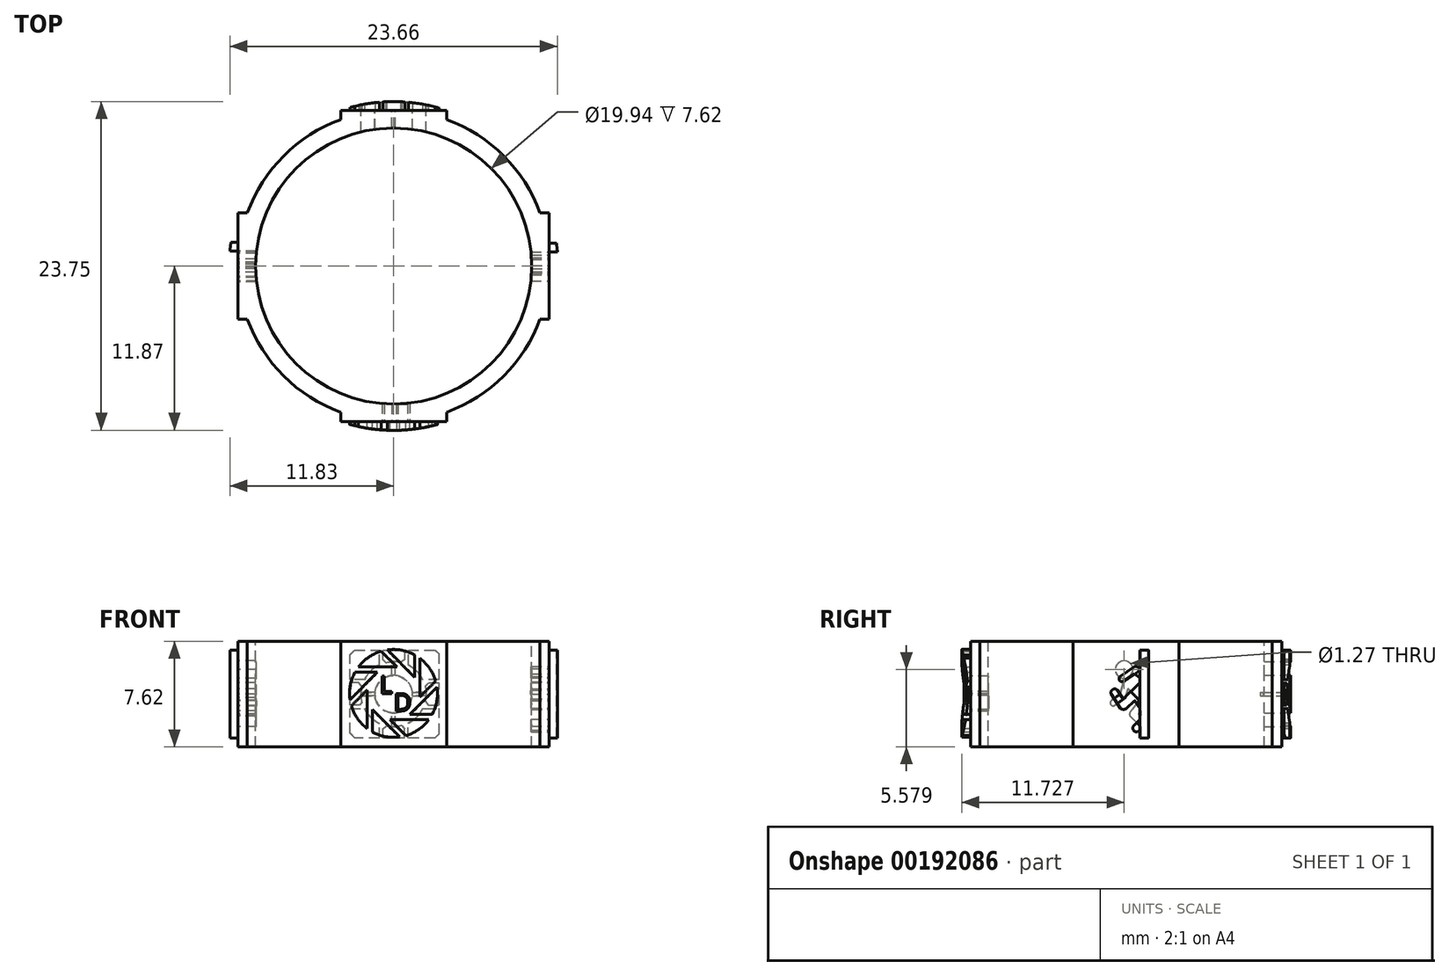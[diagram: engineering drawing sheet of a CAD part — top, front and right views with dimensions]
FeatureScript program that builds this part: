
annotation { "Feature Type Name" : "Feature", "Feature Type Description" : "" }
export const myFeature = defineFeature(function(context is Context, id is Id, definition is map)
    precondition{}
    {
        {
            var Q0;
            Q0=qCreatedBy(makeId("Front.planeOp"),FACE);
            var sketch = newSketch(context, id + "F0", { "sketchPlane" : qUnion([Q0])});
            skLineSegment(sketch, "E0.bottom", {"start": v(-11.24, 3.81) * mm, "end": v(11.24, 3.81) * mm});
            skLineSegment(sketch, "E0.top", {"start": v(-11.24, -3.81) * mm, "end": v(11.24, -3.81) * mm});
            skLineSegment(sketch, "E0.left", {"start": v(-11.24, 3.81) * mm, "end": v(-11.24, -3.81) * mm});
            skLineSegment(sketch, "E0.right", {"start": v(11.24, 3.81) * mm, "end": v(11.24, -3.81) * mm});
            skLineSegment(sketch, "E1.0", {"start": v(-2.54, 1.9) * mm, "end": v(0.25, 1.9) * mm});
            skLineSegment(sketch, "E1.1", {"start": v(0.79, 1.9) * mm, "end": v(1.52, 1.17) * mm});
            skLineSegment(sketch, "E1.2", {"start": v(1.9, 0.79) * mm, "end": v(1.9, -0.25) * mm});
            skLineSegment(sketch, "E1.3", {"start": v(1.9, -0.79) * mm, "end": v(1.17, -1.52) * mm});
            skLineSegment(sketch, "E1.4", {"start": v(0.79, -1.9) * mm, "end": v(-0.25, -1.9) * mm});
            skLineSegment(sketch, "E1.5", {"start": v(-0.79, -1.9) * mm, "end": v(-1.52, -1.17) * mm});
            skLineSegment(sketch, "E1.6", {"start": v(-1.9, -0.79) * mm, "end": v(-1.9, 0.25) * mm});
            skLineSegment(sketch, "E1.7", {"start": v(-1.9, 0.79) * mm, "end": v(-1.17, 1.52) * mm});
            skArc(sketch, "E2", {"start": v(-2.79, 1.52) * mm, "mid": v(-3.12, 0.57) * mm, "end": v(-3.14, -0.45) * mm});
            skLineSegment(sketch, "E3.0", {"start": v(-2.79, 1.52) * mm, "end": v(-1.17, 1.52) * mm});
            skLineSegment(sketch, "E4.1.0", {"start": v(-3.05, -0.9) * mm, "end": v(-1.9, 0.25) * mm});
            skLineSegment(sketch, "E4.1.1", {"start": v(-3.14, -0.45) * mm, "end": v(-1.17, 1.52) * mm});
            skLineSegment(sketch, "E4.2.0", {"start": v(-1.52, -2.79) * mm, "end": v(-1.52, -1.17) * mm});
            skLineSegment(sketch, "E4.2.1", {"start": v(-1.9, -2.54) * mm, "end": v(-1.9, 0.25) * mm});
            skLineSegment(sketch, "E4.3.0", {"start": v(0.9, -3.05) * mm, "end": v(-0.25, -1.9) * mm});
            skLineSegment(sketch, "E4.3.1", {"start": v(0.45, -3.14) * mm, "end": v(-1.52, -1.17) * mm});
            skLineSegment(sketch, "E4.4.0", {"start": v(2.79, -1.52) * mm, "end": v(1.17, -1.52) * mm});
            skLineSegment(sketch, "E4.4.1", {"start": v(2.54, -1.9) * mm, "end": v(-0.25, -1.9) * mm});
            skLineSegment(sketch, "E4.5.0", {"start": v(3.05, 0.9) * mm, "end": v(1.9, -0.25) * mm});
            skLineSegment(sketch, "E4.5.1", {"start": v(3.14, 0.45) * mm, "end": v(1.17, -1.52) * mm});
            skLineSegment(sketch, "E4.6.0", {"start": v(1.52, 2.79) * mm, "end": v(1.52, 1.17) * mm});
            skLineSegment(sketch, "E4.6.1", {"start": v(1.9, 2.54) * mm, "end": v(1.9, -0.25) * mm});
            skLineSegment(sketch, "E4.7.0", {"start": v(-0.9, 3.05) * mm, "end": v(0.25, 1.9) * mm});
            skLineSegment(sketch, "E4.7.1", {"start": v(-0.45, 3.14) * mm, "end": v(1.52, 1.17) * mm});
            skArc(sketch, "E5.trimOffspring", {"start": v(-0.9, 3.05) * mm, "mid": v(-1.8, 2.6) * mm, "end": v(-2.54, 1.9) * mm});
            skArc(sketch, "E6.trimOffspring", {"start": v(1.52, 2.79) * mm, "mid": v(0.57, 3.12) * mm, "end": v(-0.45, 3.14) * mm});
            skArc(sketch, "E7.trimOffspring", {"start": v(3.05, 0.9) * mm, "mid": v(2.6, 1.8) * mm, "end": v(1.9, 2.54) * mm});
            skArc(sketch, "E8.trimOffspring", {"start": v(2.79, -1.52) * mm, "mid": v(3.12, -0.57) * mm, "end": v(3.14, 0.45) * mm});
            skArc(sketch, "E9.trimOffspring", {"start": v(0.9, -3.05) * mm, "mid": v(1.8, -2.6) * mm, "end": v(2.54, -1.9) * mm});
            skArc(sketch, "E10.trimOffspring", {"start": v(-1.52, -2.79) * mm, "mid": v(-0.57, -3.12) * mm, "end": v(0.45, -3.14) * mm});
            skArc(sketch, "E11.trimOffspring", {"start": v(-3.05, -0.9) * mm, "mid": v(-2.6, -1.8) * mm, "end": v(-1.9, -2.54) * mm});
            skText(sketch, "E12", { "text": "L", "fontName": "OpenSans-Regular.ttf"});
            skText(sketch, "E13", { "text": "D", "fontName": "OpenSans-Regular.ttf"});
            const initialGuessF0  = {"E12": [-0.00099, 0, 1, 0, 0.00127], "E13": [0, -0.00127, 1, 0, 0.00127]};
            skSetInitialGuess(sketch, initialGuessF0);
            skSolve(sketch);
        }
        {
            var Q0;
            Q0=makeQuery(id+"F0.imprint","IMPRINT",FACE,{"disambiguationData":[TD([[makeQuery(id+"F0.imprint","IMPRINT",EDGE,{"derivedFrom":sQuery(id+"F0.wireOp",EDGE,"E0.bottom")}),-1.0]])]});
            var Q1;
            Q1=makeQuery(id+"F0.imprint","IMPRINT",FACE,{"disambiguationData":[TD([[makeQuery(id+"F0.imprint","IMPRINT",EDGE,{"derivedFrom":sQuery(id+"F0.wireOp",EDGE,"E13.sketch_text.stroke-7")}),1.0]])]});
            var Q2;
            Q2=makeQuery(id+"F0.imprint","IMPRINT",FACE,{"disambiguationData":[TD([[makeQuery(id+"F0.imprint","IMPRINT",EDGE,{"derivedFrom":sQuery(id+"F0.wireOp",EDGE,"E1.0")}),1.0]])]});
            var Q3;
            {var subQ0=sQuery(id+"F0.wireOp",EDGE,"E2");Q3=makeQuery(id+"F0.imprint","IMPRINT",FACE,{"disambiguationData":[TD([[makeQuery(id+"F0.imprint","IMPRINT",EDGE,{"derivedFrom":subQ0}),1.0]])]});}
            var Q4;
            {var subQ0=sQuery(id+"F0.wireOp",EDGE,"E4.1.0");Q4=makeQuery(id+"F0.imprint","IMPRINT",FACE,{"disambiguationData":[TD([[makeQuery(id+"F0.imprint","IMPRINT",EDGE,{"derivedFrom":subQ0}),-1.0]])]});}
            var Q5;
            {var subQ0=sQuery(id+"F0.wireOp",EDGE,"E4.2.0");Q5=makeQuery(id+"F0.imprint","IMPRINT",FACE,{"disambiguationData":[TD([[makeQuery(id+"F0.imprint","IMPRINT",EDGE,{"derivedFrom":subQ0}),-1.0]])]});}
            var Q6;
            {var subQ0=sQuery(id+"F0.wireOp",EDGE,"E4.3.0");Q6=makeQuery(id+"F0.imprint","IMPRINT",FACE,{"disambiguationData":[TD([[makeQuery(id+"F0.imprint","IMPRINT",EDGE,{"derivedFrom":subQ0}),-1.0]])]});}
            var Q7;
            {var subQ0=sQuery(id+"F0.wireOp",EDGE,"E4.4.0");Q7=makeQuery(id+"F0.imprint","IMPRINT",FACE,{"disambiguationData":[TD([[makeQuery(id+"F0.imprint","IMPRINT",EDGE,{"derivedFrom":subQ0}),-1.0]])]});}
            var Q8;
            {var subQ0=sQuery(id+"F0.wireOp",EDGE,"E4.5.0");Q8=makeQuery(id+"F0.imprint","IMPRINT",FACE,{"disambiguationData":[TD([[makeQuery(id+"F0.imprint","IMPRINT",EDGE,{"derivedFrom":subQ0}),-1.0]])]});}
            var Q9;
            {var subQ0=sQuery(id+"F0.wireOp",EDGE,"E4.6.0");Q9=makeQuery(id+"F0.imprint","IMPRINT",FACE,{"disambiguationData":[TD([[makeQuery(id+"F0.imprint","IMPRINT",EDGE,{"derivedFrom":subQ0}),-1.0]])]});}
            var Q10;
            Q10=makeQuery(id+"F0.imprint","IMPRINT",FACE,{"disambiguationData":[TD([[makeQuery(id+"F0.imprint","IMPRINT",EDGE,{"derivedFrom":sQuery(id+"F0.wireOp",EDGE,"E12.sketch_text.stroke-0")}),-1.0]])]});
            var Q11;
            Q11=makeQuery(id+"F0.imprint","IMPRINT",FACE,{"disambiguationData":[TD([[makeQuery(id+"F0.imprint","IMPRINT",EDGE,{"derivedFrom":sQuery(id+"F0.wireOp",EDGE,"E13.sketch_text.stroke-0")}),-1.0]])]});
            extrude(context, id + "F1", {"entities" : qUnion([Q0, Q1, Q2, Q3, Q4, Q5, Q6, Q7, Q8, Q9, Q10, Q11]), "depth" : 22.48 * mm});
        }
        {
            var Q0;
            Q0=makeQuery(id+"F1.opExtrude","CAP_FACE",FACE,{"disambiguationData":[OSD([sQuery(id+"F0.wireOp",EDGE,"E0.bottom"),sQuery(id+"F0.wireOp",EDGE,"E0.top"),sQuery(id+"F0.wireOp",EDGE,"E0.left"),sQuery(id+"F0.wireOp",EDGE,"E0.right")])],"isStart":false});
            var sketch = newSketch(context, id + "F2", { "sketchPlane" : qUnion([Q0])});
            skLineSegment(sketch, "E14.bottom", {"start": v(-11.25, 3.86) * mm, "end": v(11.23, 3.86) * mm});
            skLineSegment(sketch, "E14.top", {"start": v(-11.25, -3.76) * mm, "end": v(11.23, -3.76) * mm});
            skLineSegment(sketch, "E14.left", {"start": v(-11.25, 3.86) * mm, "end": v(-11.25, -3.76) * mm});
            skLineSegment(sketch, "E14.right", {"start": v(11.23, 3.86) * mm, "end": v(11.23, -3.76) * mm});
            skLineSegment(sketch, "E15.0", {"start": v(-2.55, 1.96) * mm, "end": v(0.24, 1.96) * mm});
            skLineSegment(sketch, "E15.1", {"start": v(0.78, 1.96) * mm, "end": v(1.52, 1.22) * mm});
            skLineSegment(sketch, "E15.2", {"start": v(1.9, 0.84) * mm, "end": v(1.9, -0.2) * mm});
            skLineSegment(sketch, "E15.3", {"start": v(1.9, -0.74) * mm, "end": v(1.16, -1.47) * mm});
            skLineSegment(sketch, "E15.4", {"start": v(0.78, -1.85) * mm, "end": v(-0.26, -1.85) * mm});
            skLineSegment(sketch, "E15.5", {"start": v(-0.8, -1.85) * mm, "end": v(-1.53, -1.12) * mm});
            skLineSegment(sketch, "E15.6", {"start": v(-1.91, -0.74) * mm, "end": v(-1.91, 0.3) * mm});
            skLineSegment(sketch, "E15.7", {"start": v(-1.91, 0.84) * mm, "end": v(-1.18, 1.58) * mm});
            skArc(sketch, "E16", {"start": v(-2.8, 1.58) * mm, "mid": v(-3.13, 0.62) * mm, "end": v(-3.15, -0.4) * mm});
            skLineSegment(sketch, "E17.0", {"start": v(-2.8, 1.58) * mm, "end": v(-1.18, 1.58) * mm});
            skLineSegment(sketch, "E18.1.0", {"start": v(-3.05, -0.84) * mm, "end": v(-1.91, 0.3) * mm});
            skLineSegment(sketch, "E18.1.1", {"start": v(-3.15, -0.4) * mm, "end": v(-1.18, 1.58) * mm});
            skLineSegment(sketch, "E18.2.0", {"start": v(-1.53, -2.73) * mm, "end": v(-1.53, -1.12) * mm});
            skLineSegment(sketch, "E18.2.1", {"start": v(-1.91, -2.49) * mm, "end": v(-1.91, 0.3) * mm});
            skLineSegment(sketch, "E18.3.0", {"start": v(0.88, -3) * mm, "end": v(-0.26, -1.85) * mm});
            skLineSegment(sketch, "E18.3.1", {"start": v(0.44, -3.1) * mm, "end": v(-1.53, -1.12) * mm});
            skLineSegment(sketch, "E18.4.0", {"start": v(2.78, -1.47) * mm, "end": v(1.16, -1.47) * mm});
            skLineSegment(sketch, "E18.4.1", {"start": v(2.53, -1.85) * mm, "end": v(-0.26, -1.85) * mm});
            skLineSegment(sketch, "E18.5.0", {"start": v(3.04, 0.94) * mm, "end": v(1.9, -0.2) * mm});
            skLineSegment(sketch, "E18.5.1", {"start": v(3.14, 0.5) * mm, "end": v(1.16, -1.47) * mm});
            skLineSegment(sketch, "E18.6.0", {"start": v(1.52, 2.84) * mm, "end": v(1.52, 1.22) * mm});
            skLineSegment(sketch, "E18.6.1", {"start": v(1.9, 2.6) * mm, "end": v(1.9, -0.2) * mm});
            skLineSegment(sketch, "E18.7.0", {"start": v(-0.9, 3.1) * mm, "end": v(0.24, 1.96) * mm});
            skLineSegment(sketch, "E18.7.1", {"start": v(-0.46, 3.2) * mm, "end": v(1.52, 1.22) * mm});
            skArc(sketch, "E19.trimOffspring", {"start": v(-0.9, 3.1) * mm, "mid": v(-1.82, 2.66) * mm, "end": v(-2.55, 1.96) * mm});
            skArc(sketch, "E20.trimOffspring", {"start": v(1.52, 2.84) * mm, "mid": v(0.56, 3.18) * mm, "end": v(-0.46, 3.2) * mm});
            skArc(sketch, "E21.trimOffspring", {"start": v(3.04, 0.94) * mm, "mid": v(2.6, 1.86) * mm, "end": v(1.9, 2.6) * mm});
            skArc(sketch, "E22.trimOffspring", {"start": v(2.78, -1.47) * mm, "mid": v(3.12, -0.51) * mm, "end": v(3.14, 0.5) * mm});
            skArc(sketch, "E23.trimOffspring", {"start": v(0.88, -3) * mm, "mid": v(1.8, -2.56) * mm, "end": v(2.53, -1.85) * mm});
            skArc(sketch, "E24.trimOffspring", {"start": v(-1.53, -2.73) * mm, "mid": v(-0.57, -3.07) * mm, "end": v(0.44, -3.1) * mm});
            skArc(sketch, "E25.trimOffspring", {"start": v(-3.05, -0.84) * mm, "mid": v(-2.62, -1.76) * mm, "end": v(-1.91, -2.49) * mm});
            skText(sketch, "E26", { "text": "L", "fontName": "OpenSans-Regular.ttf"});
            skText(sketch, "E27", { "text": "D", "fontName": "OpenSans-Regular.ttf"});
            const initialGuessF2  = {"E26": [-0.001, 5e-05, 1, 0, 0.00127], "E27": [0, -0.00122, 1, 0, 0.00127]};
            skSetInitialGuess(sketch, initialGuessF2);
            skSolve(sketch);
        }
        {
            var Q0;
            {var subQ0=sQuery(id+"F2.wireOp",EDGE,"E16");Q0=makeQuery(id+"F2.imprint","IMPRINT",FACE,{"disambiguationData":[TD([[makeQuery(id+"F2.imprint","IMPRINT",EDGE,{"derivedFrom":subQ0}),1.0]])]});}
            var Q1;
            Q1=makeQuery(id+"F2.imprint","IMPRINT",FACE,{"disambiguationData":[TD([[makeQuery(id+"F2.imprint","IMPRINT",EDGE,{"derivedFrom":sQuery(id+"F2.wireOp",EDGE,"E15.0")}),1.0]])]});
            var Q2;
            {var subQ0=sQuery(id+"F2.wireOp",EDGE,"E18.6.0");Q2=makeQuery(id+"F2.imprint","IMPRINT",FACE,{"disambiguationData":[TD([[makeQuery(id+"F2.imprint","IMPRINT",EDGE,{"derivedFrom":subQ0}),-1.0]])]});}
            var Q3;
            {var subQ0=sQuery(id+"F2.wireOp",EDGE,"E18.5.0");Q3=makeQuery(id+"F2.imprint","IMPRINT",FACE,{"disambiguationData":[TD([[makeQuery(id+"F2.imprint","IMPRINT",EDGE,{"derivedFrom":subQ0}),-1.0]])]});}
            var Q4;
            {var subQ0=sQuery(id+"F2.wireOp",EDGE,"E18.4.0");Q4=makeQuery(id+"F2.imprint","IMPRINT",FACE,{"disambiguationData":[TD([[makeQuery(id+"F2.imprint","IMPRINT",EDGE,{"derivedFrom":subQ0}),-1.0]])]});}
            var Q5;
            {var subQ0=sQuery(id+"F2.wireOp",EDGE,"E18.3.0");Q5=makeQuery(id+"F2.imprint","IMPRINT",FACE,{"disambiguationData":[TD([[makeQuery(id+"F2.imprint","IMPRINT",EDGE,{"derivedFrom":subQ0}),-1.0]])]});}
            var Q6;
            {var subQ0=sQuery(id+"F2.wireOp",EDGE,"E18.2.0");Q6=makeQuery(id+"F2.imprint","IMPRINT",FACE,{"disambiguationData":[TD([[makeQuery(id+"F2.imprint","IMPRINT",EDGE,{"derivedFrom":subQ0}),-1.0]])]});}
            var Q7;
            {var subQ0=sQuery(id+"F2.wireOp",EDGE,"E18.1.0");Q7=makeQuery(id+"F2.imprint","IMPRINT",FACE,{"disambiguationData":[TD([[makeQuery(id+"F2.imprint","IMPRINT",EDGE,{"derivedFrom":subQ0}),-1.0]])]});}
            var Q8;
            Q8=makeQuery(id+"F2.imprint","IMPRINT",FACE,{"disambiguationData":[TD([[makeQuery(id+"F2.imprint","IMPRINT",EDGE,{"derivedFrom":sQuery(id+"F2.wireOp",EDGE,"E26.sketch_text.stroke-0")}),-1.0]])]});
            var Q9;
            Q9=makeQuery(id+"F2.imprint","IMPRINT",FACE,{"disambiguationData":[TD([[makeQuery(id+"F2.imprint","IMPRINT",EDGE,{"derivedFrom":sQuery(id+"F2.wireOp",EDGE,"E27.sketch_text.stroke-0")}),-1.0]])]});
            extrude(context, id + "F3", {"entities" : qUnion([Q0, Q1, Q2, Q3, Q4, Q5, Q6, Q7, Q8, Q9]), "operationType" : NewBodyOperationType.ADD, "depth" : 25.4 * mm});
        }
        {
            var Q0;
            Q0=makeQuery(id+"F1.opExtrude","SWEPT_FACE",FACE,{"disambiguationData":[OSD([sQuery(id+"F0.wireOp",EDGE,"E0.right")])]});
            var sketch = newSketch(context, id + "F4", { "sketchPlane" : qUnion([Q0])});
            skLineSegment(sketch, "E28", {"start": v(-10.23, -2.6) * mm, "end": v(-10.45, -2.73) * mm});
            skLineSegment(sketch, "E29", {"start": v(-10.71, -2.31) * mm, "end": v(-10.23, -1.82) * mm});
            skLineSegment(sketch, "E30", {"start": v(-10.23, -1.82) * mm, "end": v(-10.23, -1.02) * mm});
            skLineSegment(sketch, "E31", {"start": v(-10.23, -1.02) * mm, "end": v(-10.63, -0.46) * mm});
            skLineSegment(sketch, "E32", {"start": v(-10.63, -0.46) * mm, "end": v(-11.22, -1.04) * mm});
            skLineSegment(sketch, "E33", {"start": v(-11.65, -1.04) * mm, "end": v(-12.32, 0) * mm});
            skLineSegment(sketch, "E34", {"start": v(-11.86, 0.3) * mm, "end": v(-11.44, -0.35) * mm});
            skLineSegment(sketch, "E35", {"start": v(-11.44, -0.35) * mm, "end": v(-10.24, 0.82) * mm});
            skLineSegment(sketch, "E36", {"start": v(-10.24, 1.17) * mm, "end": v(-10.63, 1.47) * mm});
            skLineSegment(sketch, "E37", {"start": v(-10.63, 1.47) * mm, "end": v(-11.44, 0.94) * mm});
            skLineSegment(sketch, "E38", {"start": v(-11.66, 1.27) * mm, "end": v(-10.67, 1.96) * mm});
            skLineSegment(sketch, "E39", {"start": v(-10.42, 1.96) * mm, "end": v(-10.24, 1.84) * mm});
            skArc(sketch, "E40", {"start": v(-10.42, 1.96) * mm, "mid": v(-10.55, 2) * mm, "end": v(-10.67, 1.96) * mm});
            skArc(sketch, "E41", {"start": v(-11.66, 1.27) * mm, "mid": v(-11.72, 1) * mm, "end": v(-11.44, 0.94) * mm});
            skArc(sketch, "E42", {"start": v(-11.86, 0.3) * mm, "mid": v(-12.21, 0.33) * mm, "end": v(-12.32, 0) * mm});
            skArc(sketch, "E43", {"start": v(-11.65, -1.04) * mm, "mid": v(-11.43, -1.1) * mm, "end": v(-11.22, -1.04) * mm});
            skArc(sketch, "E44", {"start": v(-10.71, -2.31) * mm, "mid": v(-10.7, -2.6) * mm, "end": v(-10.45, -2.73) * mm});
            skLineSegment(sketch, "E45", {"start": v(-10.24, 1.84) * mm, "end": v(-10.24, 1.17) * mm});
            skPoint(sketch, "E46.orphan", {"position": v(-10.23, 0.82) * mm});
            skPoint(sketch, "E47.start.orphan", {"position": v(-10.23, -2.98) * mm});
            skLineSegment(sketch, "E48.trimOffspring", {"start": v(-10.23, -1.82) * mm, "end": v(-10.23, -2.6) * mm});
            skLineSegment(sketch, "E49.trimOffspring", {"start": v(-10.24, 0.82) * mm, "end": v(-10.23, -1.02) * mm});
            skSolve(sketch);
        }
        {
            var Q0;
            Q0 = qSketchRegion(id + "F4", true);
            extrude(context, id + "F5", {"entities" : qUnion([Q0]), "operationType" : NewBodyOperationType.REMOVE, "oppositeDirection" : true, "depth" : 7.62 * mm});
        }
        {
            var Q0;
            Q0=makeQuery(id+"F1.opExtrude","SWEPT_FACE",FACE,{"disambiguationData":[OSD([sQuery(id+"F0.wireOp",EDGE,"E0.left")])]});
            var sketch = newSketch(context, id + "F6", { "sketchPlane" : qUnion([Q0])});
            skLineSegment(sketch, "E50", {"start": v(10.17, 1.77) * mm, "end": v(11.45, 0.82) * mm});
            skLineSegment(sketch, "E51", {"start": v(11.45, 0.82) * mm, "end": v(11.68, 0) * mm});
            skLineSegment(sketch, "E52", {"start": v(11.68, 0) * mm, "end": v(12.33, -0.48) * mm});
            skLineSegment(sketch, "E53", {"start": v(12.07, -0.82) * mm, "end": v(11.3, -0.27) * mm});
            skLineSegment(sketch, "E54", {"start": v(11.3, -0.27) * mm, "end": v(11.1, 0.4) * mm});
            skLineSegment(sketch, "E55", {"start": v(11.1, 0.4) * mm, "end": v(10.3, -0.44) * mm});
            skLineSegment(sketch, "E56", {"start": v(10.3, -0.44) * mm, "end": v(10.95, -1.32) * mm});
            skLineSegment(sketch, "E57", {"start": v(10.95, -1.59) * mm, "end": v(10.17, -2.35) * mm});
            skLineSegment(sketch, "E58", {"start": v(10.17, -1.21) * mm, "end": v(10.33, -1.42) * mm});
            skLineSegment(sketch, "E59", {"start": v(10.33, -1.42) * mm, "end": v(10.17, -1.57) * mm});
            skCircle(sketch, "E60", {"center": v(11.38, 1.77) * mm, "radius": 0.64 * mm});
            skArc(sketch, "E61", {"start": v(12.07, -0.82) * mm, "mid": v(12.35, -0.76) * mm, "end": v(12.33, -0.48) * mm});
            skArc(sketch, "E62", {"start": v(10.95, -1.59) * mm, "mid": v(11, -1.45) * mm, "end": v(10.95, -1.32) * mm});
            skLineSegment(sketch, "E63", {"start": v(10.17, 1.77) * mm, "end": v(10.17, -1.21) * mm});
            skLineSegment(sketch, "E64", {"start": v(10.17, -2.35) * mm, "end": v(10.17, -1.57) * mm});
            skPoint(sketch, "E65.end.orphan", {"position": v(10.17, 2.98) * mm});
            skPoint(sketch, "E66.start.orphan", {"position": v(10.17, -2.97) * mm});
            skSolve(sketch);
        }
        {
            var Q0;
            Q0 = qSketchRegion(id + "F6", true);
            extrude(context, id + "F7", {"entities" : qUnion([Q0]), "operationType" : NewBodyOperationType.REMOVE, "oppositeDirection" : true, "depth" : 7.62 * mm});
        }
        {
            var Q0;
            Q0=makeQuery(id+"F1.opExtrude","SWEPT_FACE",FACE,{"disambiguationData":[OSD([sQuery(id+"F0.wireOp",EDGE,"E0.left")])]});
            var sketch = newSketch(context, id + "F8", { "sketchPlane" : qUnion([Q0])});
            skLineSegment(sketch, "E67.bottom", {"start": v(9.54, 3.18) * mm, "end": v(10.17, 3.18) * mm});
            skLineSegment(sketch, "E67.top", {"start": v(9.54, -3.17) * mm, "end": v(10.17, -3.17) * mm});
            skLineSegment(sketch, "E67.left", {"start": v(9.54, 3.18) * mm, "end": v(9.54, -3.18) * mm});
            skLineSegment(sketch, "E67.right", {"start": v(10.17, 3.18) * mm, "end": v(10.17, -3.17) * mm});
            skSolve(sketch);
        }
        {
            var Q0;
            Q0 = qSketchRegion(id + "F8", true);
            var Q1;
            Q1 = qConstructionFilter(qBodyType(qCreatedBy(id + "F8" ,EDGE), BodyType.WIRE), ConstructionObject.NO);
            extrude(context, id + "F9", {"entities" : qUnion([Q0]), "operationType" : NewBodyOperationType.ADD, "surfaceEntities" : qUnion([Q1]), "depth" : 25.4 * mm});
        }
        {
            var Q0;
            Q0=makeQuery(id+"F1.opExtrude","SWEPT_FACE",FACE,{"disambiguationData":[OSD([sQuery(id+"F0.wireOp",EDGE,"E0.right")])]});
            var sketch = newSketch(context, id + "F10", { "sketchPlane" : qUnion([Q0])});
            skLineSegment(sketch, "E68.bottom", {"start": v(-10.24, 3.17) * mm, "end": v(-9.6, 3.17) * mm});
            skLineSegment(sketch, "E68.top", {"start": v(-10.24, -3.18) * mm, "end": v(-9.6, -3.18) * mm});
            skLineSegment(sketch, "E68.left", {"start": v(-10.24, 3.17) * mm, "end": v(-10.24, -3.18) * mm});
            skLineSegment(sketch, "E68.right", {"start": v(-9.6, 3.17) * mm, "end": v(-9.6, -3.18) * mm});
            skSolve(sketch);
        }
        {
            var Q0;
            Q0 = qSketchRegion(id + "F10", true);
            extrude(context, id + "F11", {"entities" : qUnion([Q0]), "operationType" : NewBodyOperationType.ADD, "depth" : 25.4 * mm});
        }
        {
            var Q0;
            Q0=makeQuery(id+"F1.opExtrude","CAP_FACE",FACE,{"disambiguationData":[OSD([sQuery(id+"F0.wireOp",EDGE,"E0.bottom"),sQuery(id+"F0.wireOp",EDGE,"E0.top"),sQuery(id+"F0.wireOp",EDGE,"E0.left"),sQuery(id+"F0.wireOp",EDGE,"E0.right")])],"isStart":true});
            var sketch = newSketch(context, id + "F12", { "sketchPlane" : qUnion([Q0])});
            skLineSegment(sketch, "E69", {"start": v(0, 3.2) * mm, "end": v(0, -3.4) * mm, "construction": true});
            skCircle(sketch, "E70", {"center": v(0, 0) * mm, "radius": 1.36 * mm});
            skArc(sketch, "E71", {"start": v(-1.06, 2.1) * mm, "mid": v(-1.66, 1.66) * mm, "end": v(-2.1, 1.06) * mm});
            skLineSegment(sketch, "E72", {"start": v(-2.3, -0.5) * mm, "end": v(-2.52, -0.8) * mm});
            skLineSegment(sketch, "E73", {"start": v(-2.52, -0.8) * mm, "end": v(-3.29, -0.8) * mm});
            skLineSegment(sketch, "E74", {"start": v(-3.29, -0.8) * mm, "end": v(-3.29, 0.79) * mm});
            skLineSegment(sketch, "E75", {"start": v(-3.29, 0.79) * mm, "end": v(-2.5, 0.79) * mm});
            skLineSegment(sketch, "E76", {"start": v(-2.5, 0.79) * mm, "end": v(-2.28, 0.57) * mm});
            skLineSegment(sketch, "E77", {"start": v(-2.1, -1.05) * mm, "end": v(-3.29, -1.05) * mm});
            skLineSegment(sketch, "E78", {"start": v(-3.29, -1.05) * mm, "end": v(-3.29, -2.87) * mm});
            skLineSegment(sketch, "E79", {"start": v(-3.29, -2.87) * mm, "end": v(-2.98, -3.18) * mm});
            skLineSegment(sketch, "E80", {"start": v(-2.98, -3.18) * mm, "end": v(-1.05, -3.18) * mm});
            skLineSegment(sketch, "E81", {"start": v(-1.05, -3.18) * mm, "end": v(-1.05, -2.1) * mm});
            skLineSegment(sketch, "E82", {"start": v(-0.59, -2.28) * mm, "end": v(-0.78, -2.5) * mm});
            skLineSegment(sketch, "E83", {"start": v(-0.78, -2.5) * mm, "end": v(-0.78, -3.18) * mm});
            skLineSegment(sketch, "E84", {"start": v(-0.78, -3.18) * mm, "end": v(0.78, -3.18) * mm});
            skLineSegment(sketch, "E85", {"start": v(0.78, -3.18) * mm, "end": v(0.78, -2.5) * mm});
            skLineSegment(sketch, "E86", {"start": v(0.78, -2.5) * mm, "end": v(0.51, -2.3) * mm});
            skLineSegment(sketch, "E87", {"start": v(1.03, -2.11) * mm, "end": v(1.03, -3.18) * mm});
            skLineSegment(sketch, "E88", {"start": v(1.03, -3.18) * mm, "end": v(2.8, -3.18) * mm});
            skLineSegment(sketch, "E89", {"start": v(2.8, -3.18) * mm, "end": v(3.14, -2.82) * mm});
            skLineSegment(sketch, "E90", {"start": v(3.14, -2.82) * mm, "end": v(3.14, -1.06) * mm});
            skLineSegment(sketch, "E91", {"start": v(3.14, -1.06) * mm, "end": v(2.1, -1.06) * mm});
            skLineSegment(sketch, "E92", {"start": v(2.28, -0.58) * mm, "end": v(2.46, -0.8) * mm});
            skLineSegment(sketch, "E93", {"start": v(2.46, -0.8) * mm, "end": v(3.14, -0.8) * mm});
            skLineSegment(sketch, "E94", {"start": v(2.28, 0.55) * mm, "end": v(2.53, 0.83) * mm});
            skLineSegment(sketch, "E95", {"start": v(2.53, 0.83) * mm, "end": v(3.14, 0.83) * mm});
            skLineSegment(sketch, "E96", {"start": v(3.14, 0.83) * mm, "end": v(3.14, -0.8) * mm});
            skLineSegment(sketch, "E97", {"start": v(2.1, 1.06) * mm, "end": v(3.14, 1.06) * mm});
            skLineSegment(sketch, "E98", {"start": v(3.14, 1.06) * mm, "end": v(3.14, 2.85) * mm});
            skLineSegment(sketch, "E99", {"start": v(3.14, 2.85) * mm, "end": v(2.82, 3.18) * mm});
            skLineSegment(sketch, "E100", {"start": v(2.82, 3.18) * mm, "end": v(1.03, 3.18) * mm});
            skLineSegment(sketch, "E101", {"start": v(1.03, 3.18) * mm, "end": v(1.03, 2.11) * mm});
            skLineSegment(sketch, "E102", {"start": v(0.77, 3.18) * mm, "end": v(0.77, 2.49) * mm});
            skLineSegment(sketch, "E103", {"start": v(0.77, 2.49) * mm, "end": v(0.57, 2.28) * mm});
            skLineSegment(sketch, "E104", {"start": v(0.77, 3.18) * mm, "end": v(-0.82, 3.18) * mm});
            skLineSegment(sketch, "E105", {"start": v(-0.82, 3.18) * mm, "end": v(-0.82, 2.51) * mm});
            skLineSegment(sketch, "E106", {"start": v(-0.82, 2.51) * mm, "end": v(-0.52, 2.3) * mm});
            skLineSegment(sketch, "E107", {"start": v(-1.06, 2.1) * mm, "end": v(-1.06, 3.18) * mm});
            skLineSegment(sketch, "E108", {"start": v(-1.06, 3.18) * mm, "end": v(-3, 3.18) * mm});
            skLineSegment(sketch, "E109", {"start": v(-3, 3.18) * mm, "end": v(-3.29, 2.9) * mm});
            skLineSegment(sketch, "E110", {"start": v(-3.29, 2.9) * mm, "end": v(-3.29, 1.06) * mm});
            skLineSegment(sketch, "E111", {"start": v(-3.29, 1.06) * mm, "end": v(-2.1, 1.06) * mm});
            skArc(sketch, "E112.trimOffspring", {"start": v(0.57, 2.28) * mm, "mid": v(0.03, 2.35) * mm, "end": v(-0.52, 2.3) * mm});
            skArc(sketch, "E113.trimOffspring", {"start": v(2.1, 1.06) * mm, "mid": v(1.65, 1.67) * mm, "end": v(1.03, 2.11) * mm});
            skArc(sketch, "E114.trimOffspring", {"start": v(2.28, -0.58) * mm, "mid": v(2.35, -0.02) * mm, "end": v(2.28, 0.55) * mm});
            skArc(sketch, "E115.trimOffspring", {"start": v(1.03, -2.11) * mm, "mid": v(1.65, -1.67) * mm, "end": v(2.1, -1.06) * mm});
            skArc(sketch, "E116.trimOffspring", {"start": v(-0.59, -2.28) * mm, "mid": v(-0.04, -2.35) * mm, "end": v(0.51, -2.3) * mm});
            skArc(sketch, "E117.trimOffspring", {"start": v(-2.28, 0.57) * mm, "mid": v(-2.35, 0.03) * mm, "end": v(-2.3, -0.5) * mm});
            skArc(sketch, "E118.trimOffspring", {"start": v(-2.1, -1.05) * mm, "mid": v(-1.66, -1.66) * mm, "end": v(-1.05, -2.1) * mm});
            skSolve(sketch);
        }
        {
            var Q0;
            Q0 = qSketchRegion(id + "F12", true);
            extrude(context, id + "F13", {"entities" : qUnion([Q0]), "operationType" : NewBodyOperationType.ADD, "depth" : 25.4 * mm});
        }
        {
            var Q0;
            Q0=makeQuery(id+"F3.opExtrude","CAP_FACE",FACE,{"disambiguationData":[OSD([sQuery(id+"F2.wireOp",EDGE,"E26.sketch_text.stroke-0"),sQuery(id+"F2.wireOp",EDGE,"E26.sketch_text.stroke-1"),sQuery(id+"F2.wireOp",EDGE,"E26.sketch_text.stroke-2"),sQuery(id+"F2.wireOp",EDGE,"E26.sketch_text.stroke-3"),sQuery(id+"F2.wireOp",EDGE,"E26.sketch_text.stroke-4"),sQuery(id+"F2.wireOp",EDGE,"E26.sketch_text.stroke-5")])],"isStart":false});
            var Q1;
            Q1=makeQuery(id+"F3.opExtrude","CAP_FACE",FACE,{"disambiguationData":[OSD([sQuery(id+"F2.wireOp",EDGE,"E27.sketch_text.stroke-0"),sQuery(id+"F2.wireOp",EDGE,"E27.sketch_text.stroke-1"),sQuery(id+"F2.wireOp",EDGE,"E27.sketch_text.stroke-2"),sQuery(id+"F2.wireOp",EDGE,"E27.sketch_text.stroke-3"),sQuery(id+"F2.wireOp",EDGE,"E27.sketch_text.stroke-4"),sQuery(id+"F2.wireOp",EDGE,"E27.sketch_text.stroke-5"),sQuery(id+"F2.wireOp",EDGE,"E27.sketch_text.stroke-6"),sQuery(id+"F2.wireOp",EDGE,"E27.sketch_text.stroke-7"),sQuery(id+"F2.wireOp",EDGE,"E27.sketch_text.stroke-8"),sQuery(id+"F2.wireOp",EDGE,"E27.sketch_text.stroke-9"),sQuery(id+"F2.wireOp",EDGE,"E27.sketch_text.stroke-10"),sQuery(id+"F2.wireOp",EDGE,"E27.sketch_text.stroke-11"),sQuery(id+"F2.wireOp",EDGE,"E27.sketch_text.stroke-12"),sQuery(id+"F2.wireOp",EDGE,"E27.sketch_text.stroke-13")])],"isStart":false});
            extrude(context, id + "F14", {"entities" : qUnion([Q0, Q1]), "operationType" : NewBodyOperationType.REMOVE, "oppositeDirection" : true, "depth" : 33.02 * mm});
        }
        {
            var Q0;
            Q0=makeQuery(id+"F1.opExtrude","CAP_FACE",FACE,{"disambiguationData":[OSD([sQuery(id+"F0.wireOp",EDGE,"E0.bottom"),sQuery(id+"F0.wireOp",EDGE,"E0.top"),sQuery(id+"F0.wireOp",EDGE,"E0.left"),sQuery(id+"F0.wireOp",EDGE,"E0.right")])],"isStart":true});
            var sketch = newSketch(context, id + "F15", { "sketchPlane" : qUnion([Q0])});
            skArc(sketch, "E119", {"start": v(-2.35, 0.13) * mm, "mid": v(-2.35, 0.06) * mm, "end": v(-2.35, 0) * mm});
            skArc(sketch, "E120", {"start": v(-1.35, 0.13) * mm, "mid": v(-1.36, 0) * mm, "end": v(-1.35, -0.13) * mm});
            skLineSegment(sketch, "E121.0", {"start": v(-1.35, 0.13) * mm, "end": v(-2.35, 0.13) * mm});
            skArc(sketch, "E122.MirrorCS", {"start": v(-2.35, -0.13) * mm, "mid": v(-2.35, -0.06) * mm, "end": v(-2.35, 0) * mm});
            skLineSegment(sketch, "E123.MirrorCS", {"start": v(-1.35, -0.13) * mm, "end": v(-2.35, -0.13) * mm});
            skLineSegment(sketch, "E124.1.0", {"start": v(-0.13, -1.35) * mm, "end": v(-0.13, -2.35) * mm});
            skLineSegment(sketch, "E124.1.1", {"start": v(0.13, -1.35) * mm, "end": v(0.13, -2.35) * mm});
            skArc(sketch, "E124.1.2", {"start": v(0.13, -2.35) * mm, "mid": v(0.06, -2.35) * mm, "end": v(0, -2.35) * mm});
            skArc(sketch, "E124.1.3", {"start": v(-0.13, -2.35) * mm, "mid": v(-0.06, -2.35) * mm, "end": v(0, -2.35) * mm});
            skArc(sketch, "E124.1.4", {"start": v(-0.13, -1.35) * mm, "mid": v(0, -1.36) * mm, "end": v(0.13, -1.35) * mm});
            skLineSegment(sketch, "E124.2.0", {"start": v(1.35, -0.13) * mm, "end": v(2.35, -0.13) * mm});
            skLineSegment(sketch, "E124.2.1", {"start": v(1.35, 0.13) * mm, "end": v(2.35, 0.13) * mm});
            skArc(sketch, "E124.2.2", {"start": v(2.35, 0.13) * mm, "mid": v(2.35, 0.06) * mm, "end": v(2.35, 0) * mm});
            skArc(sketch, "E124.2.3", {"start": v(2.35, -0.13) * mm, "mid": v(2.35, -0.06) * mm, "end": v(2.35, 0) * mm});
            skArc(sketch, "E124.2.4", {"start": v(1.35, -0.13) * mm, "mid": v(1.36, 0) * mm, "end": v(1.35, 0.13) * mm});
            skLineSegment(sketch, "E124.3.0", {"start": v(0.13, 1.35) * mm, "end": v(0.13, 2.35) * mm});
            skLineSegment(sketch, "E124.3.1", {"start": v(-0.13, 1.35) * mm, "end": v(-0.13, 2.35) * mm});
            skArc(sketch, "E124.3.2", {"start": v(-0.13, 2.35) * mm, "mid": v(-0.06, 2.35) * mm, "end": v(0, 2.35) * mm});
            skArc(sketch, "E124.3.3", {"start": v(0.13, 2.35) * mm, "mid": v(0.06, 2.35) * mm, "end": v(0, 2.35) * mm});
            skArc(sketch, "E124.3.4", {"start": v(0.13, 1.35) * mm, "mid": v(0, 1.36) * mm, "end": v(-0.13, 1.35) * mm});
            skSolve(sketch);
        }
        {
            var Q0;
            Q0 = qSketchRegion(id + "F15", true);
            extrude(context, id + "F16", {"entities" : qUnion([Q0]), "operationType" : NewBodyOperationType.REMOVE, "oppositeDirection" : true, "depth" : 7.62 * mm});
        }
        {
            var Q0;
            Q0=makeQuery(id+"F1.opExtrude","SWEPT_FACE",FACE,{"disambiguationData":[OSD([sQuery(id+"F0.wireOp",EDGE,"E0.bottom")])]});
            var sketch = newSketch(context, id + "F17", { "sketchPlane" : qUnion([Q0])});
            skArc(sketch, "E125", {"start": v(-10.57, -15.07) * mm, "mid": v(-7.95, -19.19) * mm, "end": v(-3.83, -21.8) * mm});
            skArc(sketch, "E126", {"start": v(-3.83, -22.48) * mm, "mid": v(0, -23.11) * mm, "end": v(3.83, -22.48) * mm});
            skCircle(sketch, "E127", {"center": v(0, -11.24) * mm, "radius": 38.1 * mm});
            skCircle(sketch, "E128", {"center": v(0, -11.24) * mm, "radius": 9.97 * mm});
            skArc(sketch, "E129.trimOffspring", {"start": v(-11.24, -7.4) * mm, "mid": v(-11.87, -11.24) * mm, "end": v(-11.24, -15.07) * mm});
            skArc(sketch, "E130.trimOffspring", {"start": v(3.83, 0) * mm, "mid": v(0, 0.64) * mm, "end": v(-3.83, 0) * mm});
            skArc(sketch, "E131.trimOffspring", {"start": v(11.24, -15.07) * mm, "mid": v(11.87, -11.24) * mm, "end": v(11.24, -7.4) * mm});
            skLineSegment(sketch, "E132", {"start": v(-3.83, 0) * mm, "end": v(-3.83, -0.67) * mm});
            skLineSegment(sketch, "E133", {"start": v(3.83, 0) * mm, "end": v(3.83, -0.67) * mm});
            skLineSegment(sketch, "E134", {"start": v(11.24, -7.4) * mm, "end": v(10.57, -7.4) * mm});
            skLineSegment(sketch, "E135", {"start": v(11.24, -15.07) * mm, "end": v(10.57, -15.07) * mm});
            skLineSegment(sketch, "E136", {"start": v(3.83, -22.48) * mm, "end": v(3.83, -21.8) * mm});
            skLineSegment(sketch, "E137", {"start": v(-3.83, -22.48) * mm, "end": v(-3.83, -21.8) * mm});
            skLineSegment(sketch, "E138", {"start": v(-11.24, -15.07) * mm, "end": v(-10.57, -15.07) * mm});
            skLineSegment(sketch, "E139", {"start": v(-11.24, -7.4) * mm, "end": v(-10.57, -7.4) * mm});
            skPoint(sketch, "E140.start.orphan", {"position": v(-11.24, -11.24) * mm});
            skArc(sketch, "E141.trimOffspring", {"start": v(-3.83, -0.67) * mm, "mid": v(-7.95, -3.3) * mm, "end": v(-10.57, -7.4) * mm});
            skPoint(sketch, "E142.start.orphan", {"position": v(0, 0) * mm});
            skArc(sketch, "E143.trimOffspring", {"start": v(10.57, -7.4) * mm, "mid": v(7.95, -3.3) * mm, "end": v(3.83, -0.67) * mm});
            skPoint(sketch, "E144.start.orphan", {"position": v(11.24, -11.24) * mm});
            skArc(sketch, "E145.trimOffspring", {"start": v(3.83, -21.8) * mm, "mid": v(7.95, -19.19) * mm, "end": v(10.57, -15.07) * mm});
            skPoint(sketch, "E146.start.orphan", {"position": v(0, -22.48) * mm});
            skSolve(sketch);
        }
        {
            var Q0;
            {var subQ12=sQuery(id+"F17.wireOp",EDGE,"E126");Q0=makeQuery(id+"F17.imprint","IMPRINT",FACE,{"disambiguationData":[TD([[makeQuery(id+"F17.imprint","IMPRINT",EDGE,{"derivedFrom":subQ12}),-1.0]])]});}
            var Q1;
            Q1=makeQuery(id+"F17.imprint","IMPRINT",FACE,{"disambiguationData":[TD([[makeQuery(id+"F17.imprint","IMPRINT",EDGE,{"derivedFrom":sQuery(id+"F17.wireOp",EDGE,"E128")}),1.0]])]});
            var Q2;
            {var subQ5=sQuery(id+"F17.wireOp",EDGE,"E132");Q2=makeQuery(id+"F17.imprint","IMPRINT",FACE,{"disambiguationData":[TD([[makeQuery(id+"F17.imprint","IMPRINT",EDGE,{"derivedFrom":subQ5}),-1.0]])]});}
            var Q3;
            {var subQ5=sQuery(id+"F17.wireOp",EDGE,"E133");Q3=makeQuery(id+"F17.imprint","IMPRINT",FACE,{"disambiguationData":[TD([[makeQuery(id+"F17.imprint","IMPRINT",EDGE,{"derivedFrom":subQ5}),1.0]])]});}
            var Q4;
            {var subQ5=sQuery(id+"F17.wireOp",EDGE,"E135");Q4=makeQuery(id+"F17.imprint","IMPRINT",FACE,{"disambiguationData":[TD([[makeQuery(id+"F17.imprint","IMPRINT",EDGE,{"derivedFrom":subQ5}),1.0]])]});}
            var Q5;
            Q5=makeQuery(id+"F17.imprint","IMPRINT",FACE,{"disambiguationData":[TD([[makeQuery(id+"F17.imprint","IMPRINT",EDGE,{"derivedFrom":sQuery(id+"F17.wireOp",EDGE,"E125")}),-1.0]])]});
            extrude(context, id + "F18", {"entities" : qUnion([Q0, Q1, Q2, Q3, Q4, Q5]), "operationType" : NewBodyOperationType.REMOVE, "endBound" : BoundingType.THROUGH_ALL, "oppositeDirection" : true, "depth" : 25.4 * mm});
        }
    });
